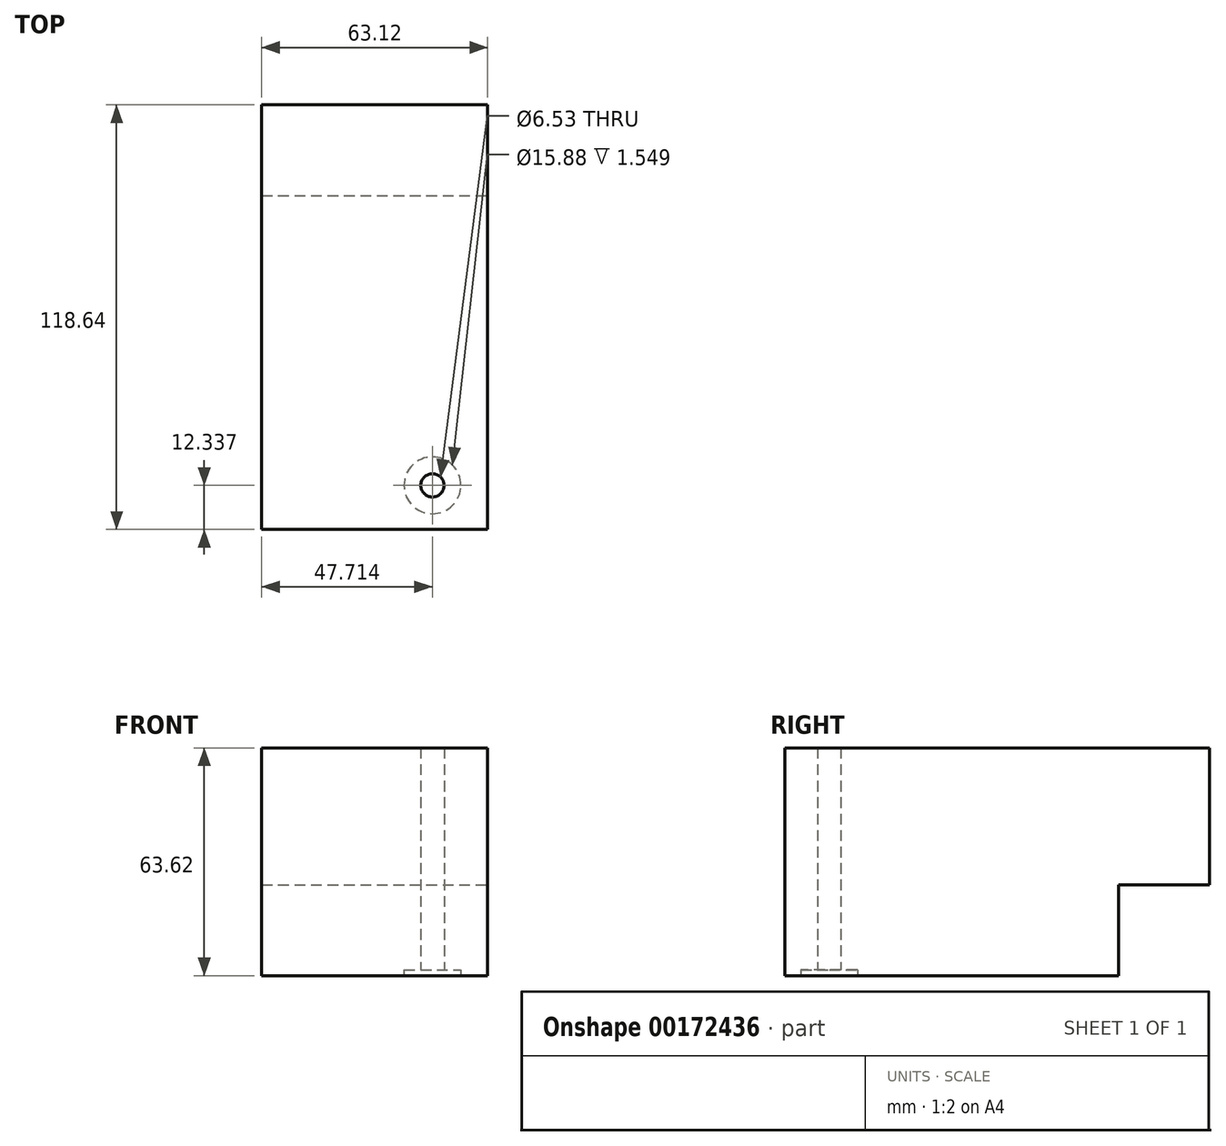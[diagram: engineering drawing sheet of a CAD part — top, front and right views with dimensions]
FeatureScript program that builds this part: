
annotation { "Feature Type Name" : "Feature", "Feature Type Description" : "" }
export const myFeature = defineFeature(function(context is Context, id is Id, definition is map)
    precondition{}
    {
        {
            var Q0;
            Q0=qCreatedBy(makeId("Front.planeOp"),FACE);
            var sketch = newSketch(context, id + "F0", { "sketchPlane" : qUnion([Q0])});
            skLineSegment(sketch, "E0", {"start": v(-39.92, 41.65) * mm, "end": v(-39.92, -21.97) * mm});
            skLineSegment(sketch, "E1", {"start": v(-39.92, 41.65) * mm, "end": v(23.2, 41.65) * mm});
            skLineSegment(sketch, "E2", {"start": v(23.2, 41.65) * mm, "end": v(23.2, -21.97) * mm});
            skLineSegment(sketch, "E3", {"start": v(-39.92, -21.97) * mm, "end": v(23.2, -21.97) * mm});
            skSolve(sketch);
        }
        {
            var Q0;
            Q0 = qSketchRegion(id + "F0", true);
            var Q1;
            Q1 = qSketchRegion(id + "FJY9AK5rwycX40Q_1", true);
            extrude(context, id + "F1", {"entities" : qUnion([Q0, Q1]), "depth" : 118.64 * mm});
        }
        {
            var Q0;
            Q0=makeQuery(id+"F1.opExtrude","SWEPT_FACE",FACE,{"disambiguationData":[OSD([sQuery(id+"F0.wireOp",EDGE,"E2")])]});
            var sketch = newSketch(context, id + "F2", { "sketchPlane" : qUnion([Q0])});
            skLineSegment(sketch, "E4", {"start": v(-25.4, -21.97) * mm, "end": v(-25.4, 3.43) * mm});
            skLineSegment(sketch, "E5", {"start": v(-25.4, 3.43) * mm, "end": v(0, 3.43) * mm});
            skLineSegment(sketch, "E6.0", {"start": v(0, 3.43) * mm, "end": v(0, -21.97) * mm});
            skLineSegment(sketch, "E7.0", {"start": v(-25.4, -21.97) * mm, "end": v(0, -21.97) * mm});
            skPoint(sketch, "E8.orphan", {"position": v(0, 41.65) * mm});
            skPoint(sketch, "E9.orphan", {"position": v(-118.64, -21.97) * mm});
            skSolve(sketch);
        }
        {
            var Q0;
            Q0=makeQuery(id+"F2.imprint","IMPRINT",FACE,{"disambiguationData":[TD([[makeQuery(id+"F2.imprint","IMPRINT",EDGE,{"derivedFrom":sQuery(id+"F2.wireOp",EDGE,"E4")}),-1.0]])]});
            extrude(context, id + "F3", {"entities" : qUnion([Q0]), "operationType" : NewBodyOperationType.REMOVE, "endBound" : BoundingType.UP_TO_NEXT, "oppositeDirection" : true, "depth" : 25.4 * mm});
        }
        {
            var Q0;
            Q0=makeQuery(id+"F1.opExtrude","SWEPT_FACE",FACE,{"disambiguationData":[OSD([sQuery(id+"F0.wireOp",EDGE,"E3")])]});
            var sketch = newSketch(context, id + "F4", { "sketchPlane" : qUnion([Q0])});
            skCircle(sketch, "E10", {"center": v(7.8, 106.3) * mm, "radius": 3.26 * mm});
            skSolve(sketch);
        }
        {
            var Q0;
            Q0 = qSketchRegion(id + "F4", true);
            extrude(context, id + "F5", {"entities" : qUnion([Q0]), "operationType" : NewBodyOperationType.REMOVE, "endBound" : BoundingType.UP_TO_NEXT, "oppositeDirection" : true, "depth" : 57.16 * mm});
        }
        {
            var Q0;
            Q0=makeQuery(id+"F1.opExtrude","SWEPT_FACE",FACE,{"disambiguationData":[OSD([sQuery(id+"F0.wireOp",EDGE,"E3")])]});
            var sketch = newSketch(context, id + "F6", { "sketchPlane" : qUnion([Q0])});
            skCircle(sketch, "E11", {"center": v(7.8, 106.3) * mm, "radius": 7.94 * mm});
            skSolve(sketch);
        }
        {
            var Q0;
            Q0 = qSketchRegion(id + "F6", true);
            extrude(context, id + "F7", {"entities" : qUnion([Q0]), "operationType" : NewBodyOperationType.REMOVE, "oppositeDirection" : true, "depth" : 1.55 * mm});
        }
    });
